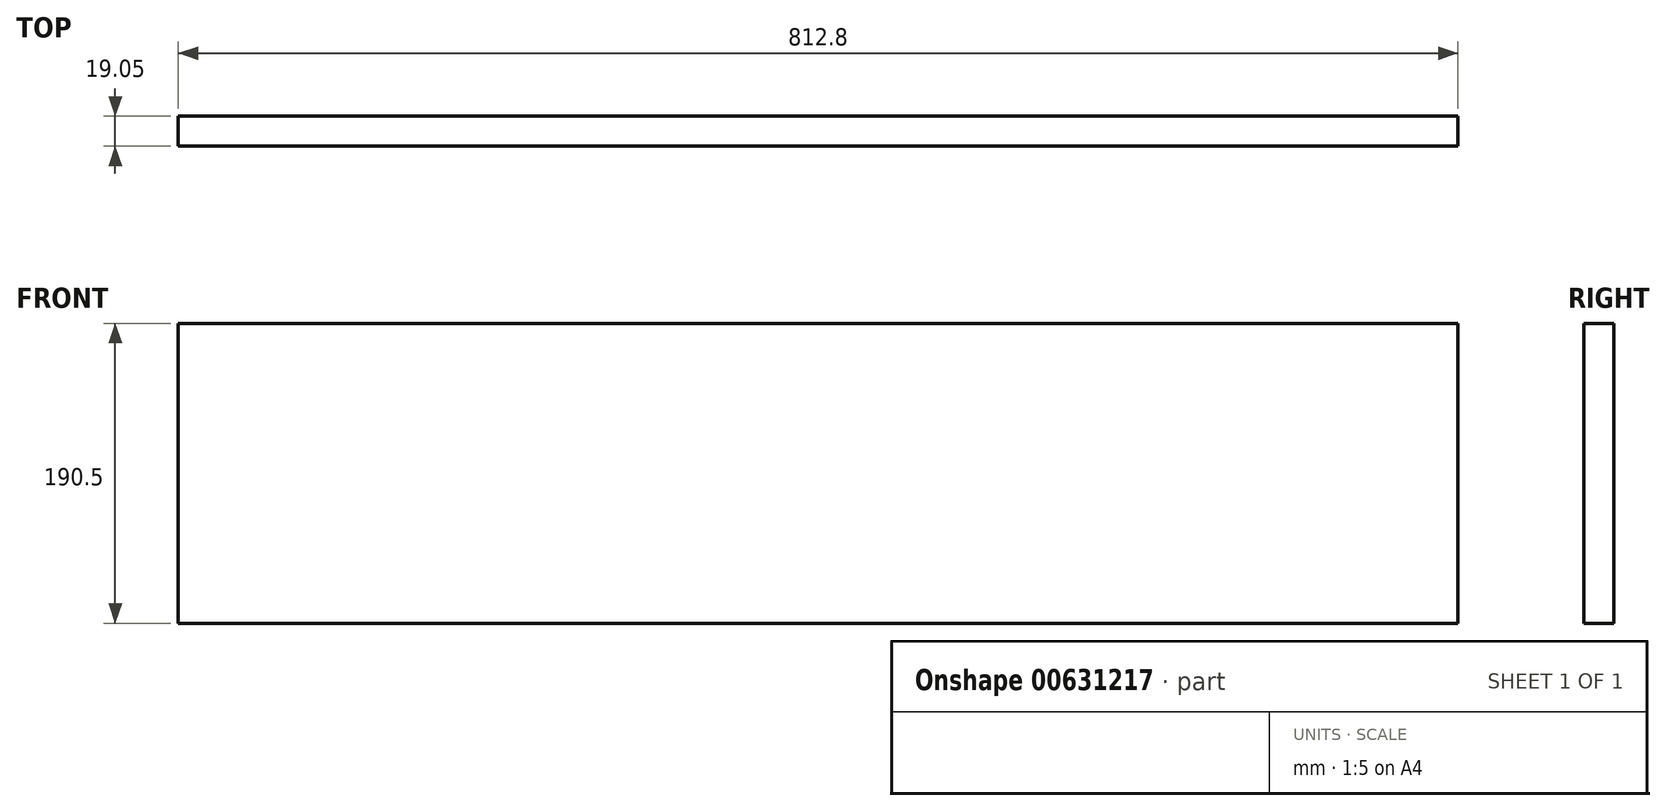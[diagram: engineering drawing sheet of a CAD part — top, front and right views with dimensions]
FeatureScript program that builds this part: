
annotation { "Feature Type Name" : "Feature", "Feature Type Description" : "" }
export const myFeature = defineFeature(function(context is Context, id is Id, definition is map)
    precondition{}
    {
        {
            var Q0;
            Q0=qCreatedBy(makeId("Front.planeOp"),FACE);
            var sketch = newSketch(context, id + "F0", { "sketchPlane" : qUnion([Q0])});
            skLineSegment(sketch, "E0.bottom", {"start": v(0, 0) * mm, "end": v(812.8, 0) * mm});
            skLineSegment(sketch, "E0.top", {"start": v(0, 190.5) * mm, "end": v(812.8, 190.5) * mm});
            skLineSegment(sketch, "E0.left", {"start": v(0, 0) * mm, "end": v(0, 190.5) * mm});
            skLineSegment(sketch, "E0.right", {"start": v(812.8, 0) * mm, "end": v(812.8, 190.5) * mm});
            skSolve(sketch);
        }
        {
            var Q0;
            Q0 = qSketchRegion(id + "Fzz42SO8jX8z24B_0", true);
            var Q1;
            Q1=makeQuery(id+"F0.imprint","IMPRINT",FACE,{"disambiguationData":[TD([[makeQuery(id+"F0.imprint","IMPRINT",EDGE,{"derivedFrom":sQuery(id+"F0.wireOp",EDGE,"E0.bottom")}),1.0]])]});
            extrude(context, id + "F1", {"entities" : qUnion([Q0, Q1]), "depth" : -19.05 * mm, "offsetDistance" : 25.4 * mm});
        }
    });
